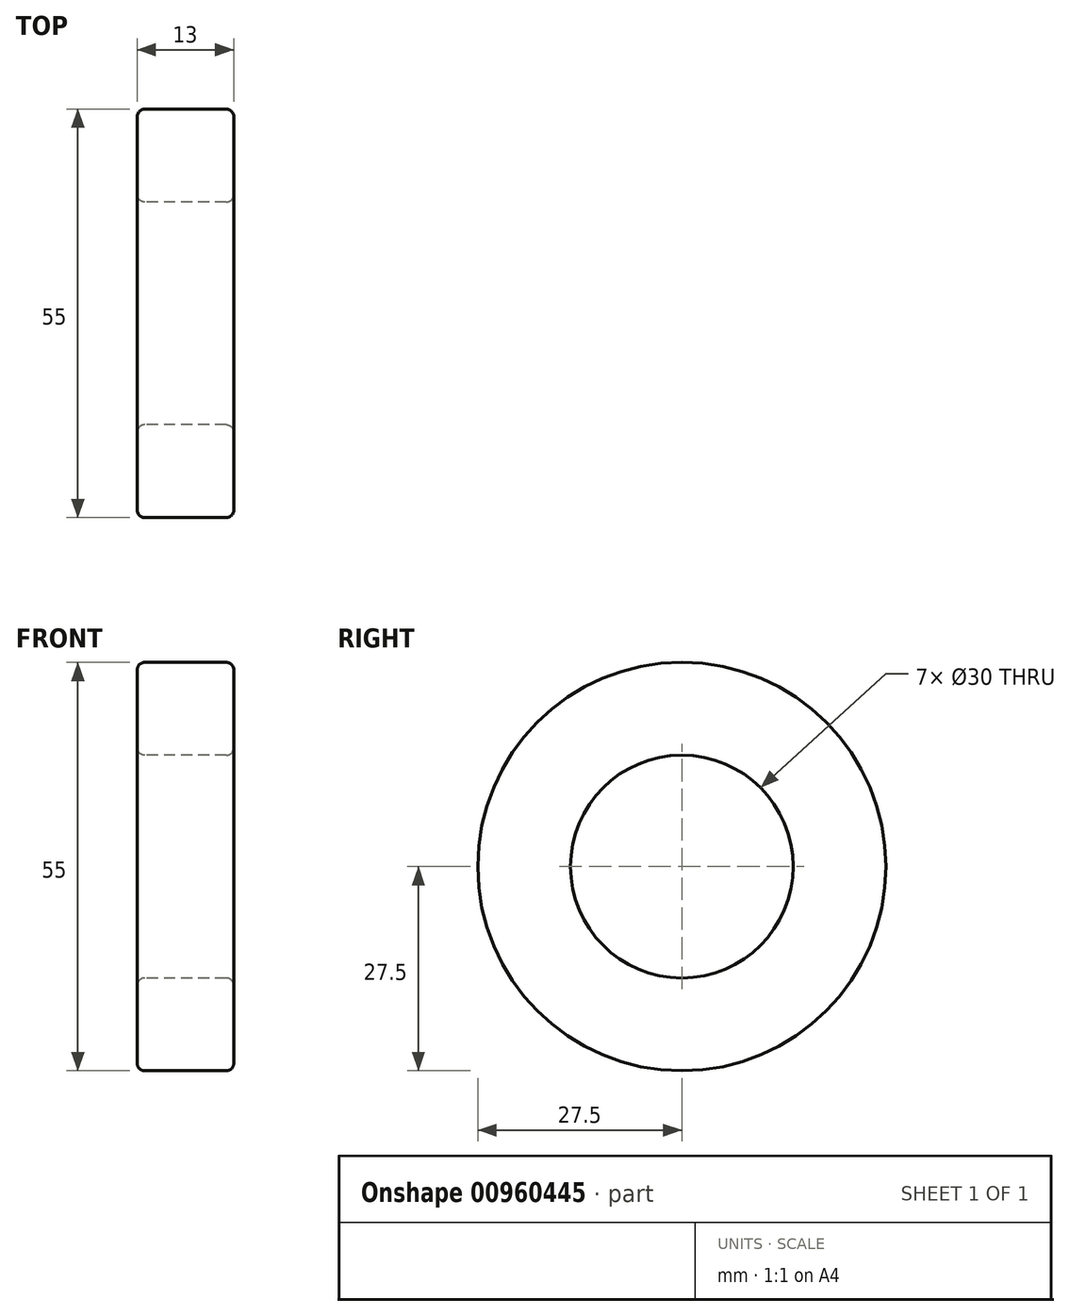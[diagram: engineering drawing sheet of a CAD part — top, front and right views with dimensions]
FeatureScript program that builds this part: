
annotation { "Feature Type Name" : "Feature", "Feature Type Description" : "" }
export const myFeature = defineFeature(function(context is Context, id is Id, definition is map)
    precondition{}
    {
        {
            var Q0;
            Q0=qCreatedBy(makeId("Front.planeOp"),FACE);
            var sketch = newSketch(context, id + "F0", { "sketchPlane" : qUnion([Q0])});
            skLineSegment(sketch, "E0.bottom", {"start": v(13, 27.5) * mm, "end": v(0, 27.5) * mm});
            skLineSegment(sketch, "E0.top", {"start": v(13, 15) * mm, "end": v(0, 15) * mm});
            skLineSegment(sketch, "E0.left", {"start": v(13, 27.5) * mm, "end": v(13, 15) * mm});
            skLineSegment(sketch, "E0.right", {"start": v(0, 27.5) * mm, "end": v(0, 15) * mm});
            skLineSegment(sketch, "E1", {"start": v(0, 0) * mm, "end": v(14, 0) * mm});
            skSolve(sketch);
        }
        {
            var Q0;
            Q0 = qSketchRegion(id + "F0", true);
            var Q1;
            Q1=sQuery(id+"F0.wireOp",EDGE,"E1");
            revolve(context, id + "F1", {"surfaceOperationType" : NewSurfaceOperationType.NEW, "entities" : qUnion([Q0]), "axis" : qUnion([Q1]), "revolveType" : RevolveType.FULL});
        }
        {
            var Q0;
            Q0=makeQuery(id+"F1.opRevolve","SWEPT_FACE",FACE,{"disambiguationData":[OSD([sQuery(id+"F0.wireOp",EDGE,"E0.bottom")])]});
            var Q1;
            Q1=makeQuery(id+"F1.opRevolve","SWEPT_FACE",FACE,{"disambiguationData":[OSD([sQuery(id+"F0.wireOp",EDGE,"E0.top")])]});
            fillet(context, id + "F2", {"entities" : qUnion([Q0, Q1]), "radius" : 1 * mm, "tangentPropagation" : true, "allowEdgeOverflow" : false});
        }
    });
